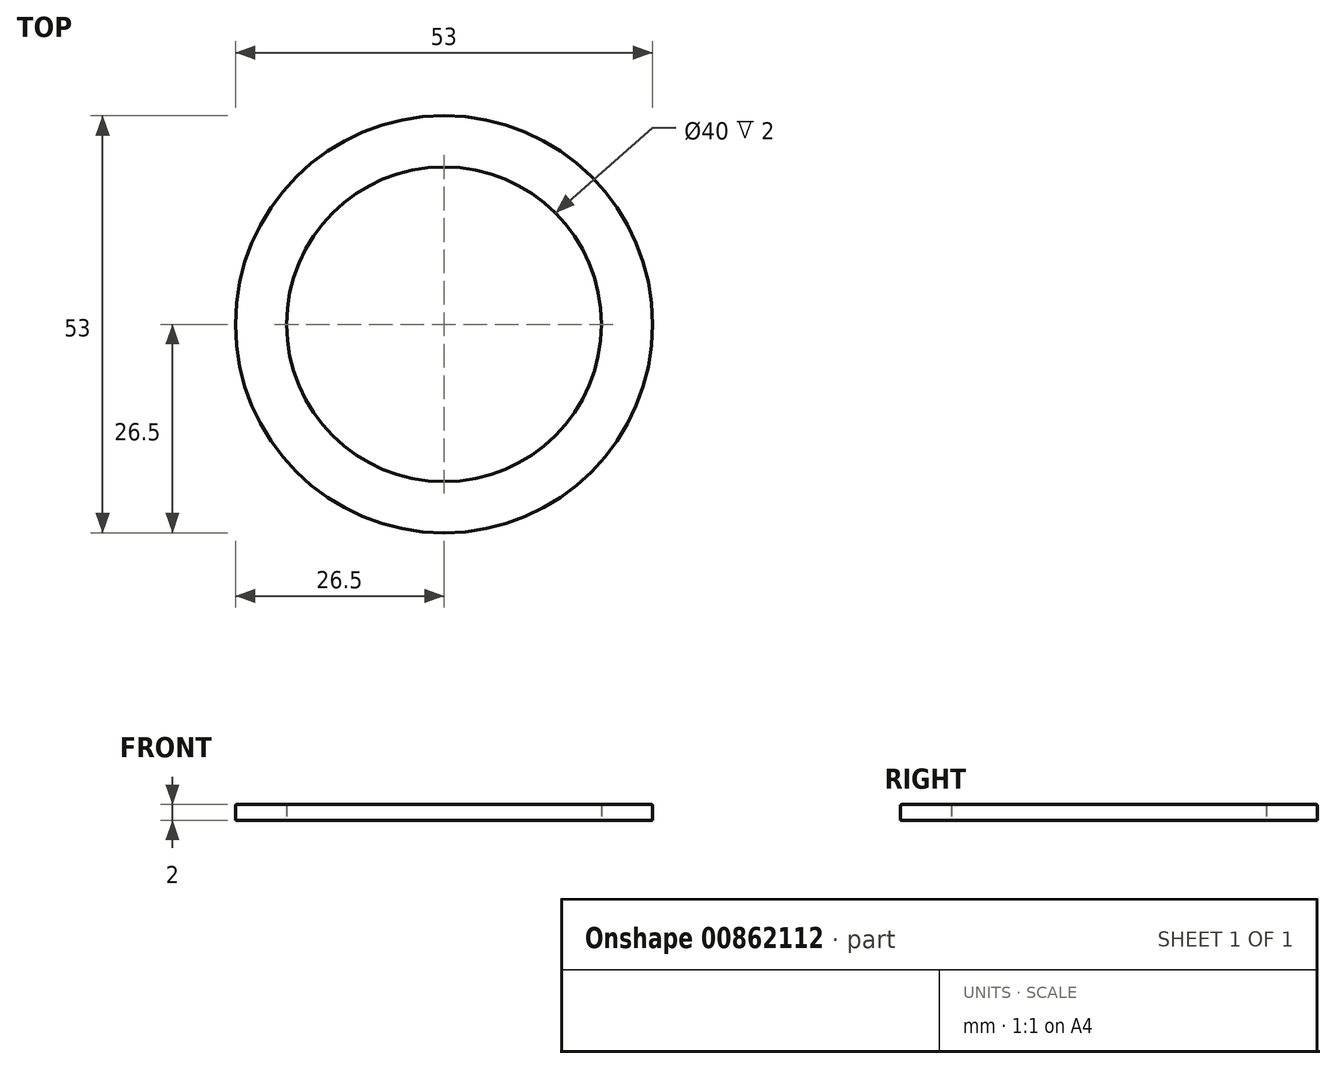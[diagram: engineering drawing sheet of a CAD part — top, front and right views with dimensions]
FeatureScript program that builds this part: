
annotation { "Feature Type Name" : "Feature", "Feature Type Description" : "" }
export const myFeature = defineFeature(function(context is Context, id is Id, definition is map)
    precondition{}
    {
        {
            var Q0;
            Q0=qCreatedBy(makeId("Top.planeOp"),FACE);
            var sketch = newSketch(context, id + "F0", { "sketchPlane" : qUnion([Q0])});
            skCircle(sketch, "E0", {"center": v(0, 0) * mm, "radius": 26.5 * mm});
            skSolve(sketch);
        }
        {
            var Q0;
            Q0 = qSketchRegion(id + "F0", true);
            extrude(context, id + "F1", {"entities" : qUnion([Q0]), "depth" : 2 * mm, "offsetDistance" : 25 * mm});
        }
        {
            var Q0;
            Q0=qCreatedBy(makeId("Top.planeOp"),FACE);
            var sketch = newSketch(context, id + "F2", { "sketchPlane" : qUnion([Q0])});
            skCircle(sketch, "E1", {"center": v(0, 0) * mm, "radius": 20 * mm});
            skSolve(sketch);
        }
        {
            var Q0;
            Q0 = qSketchRegion(id + "F2", true);
            extrude(context, id + "F3", {"entities" : qUnion([Q0]), "operationType" : NewBodyOperationType.REMOVE, "depth" : 2 * mm, "offsetDistance" : 25 * mm});
        }
        {
            var Q0;
            Q0=makeQuery(id+"F1.opExtrude","CAP_EDGE",EDGE,{"disambiguationData":[OSD([sQuery(id+"F0.wireOp",EDGE,"E0")])],"isStart":false});
            var Q1;
            Q1=makeQuery(id+"F3.boolean.opBoolean","COPY",EDGE,{"derivedFrom":makeQuery(id+"F3.opExtrude","CAP_EDGE",EDGE,{"disambiguationData":[OSD([sQuery(id+"F2.wireOp",EDGE,"E1")])],"isStart":false})});
            fillet(context, id + "F4", {"entities" : qUnion([Q0, Q1]), "radius" : 0.2 * mm, "tangentPropagation" : true, "allowEdgeOverflow" : false});
        }
    });
